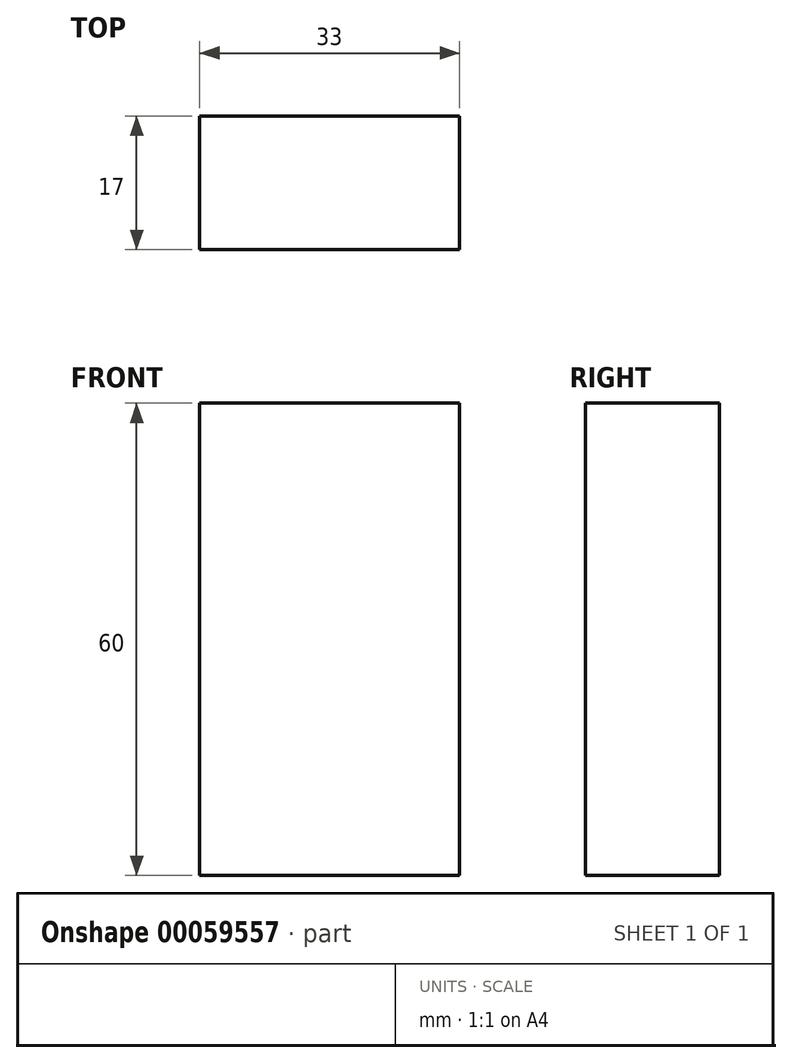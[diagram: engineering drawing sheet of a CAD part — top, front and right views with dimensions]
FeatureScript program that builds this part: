
annotation { "Feature Type Name" : "Feature", "Feature Type Description" : "" }
export const myFeature = defineFeature(function(context is Context, id is Id, definition is map)
    precondition{}
    {
        {
            var Q0;
            Q0=qCreatedBy(makeId("Front.planeOp"),FACE);
            var sketch = newSketch(context, id + "F0", { "sketchPlane" : qUnion([Q0])});
            skLineSegment(sketch, "E0.bottom", {"start": v(-16.5, 30) * mm, "end": v(16.5, 30) * mm});
            skLineSegment(sketch, "E0.top", {"start": v(-16.5, -30) * mm, "end": v(16.5, -30) * mm});
            skLineSegment(sketch, "E0.left", {"start": v(-16.5, 30) * mm, "end": v(-16.5, -30) * mm});
            skLineSegment(sketch, "E0.right", {"start": v(16.5, 30) * mm, "end": v(16.5, -30) * mm});
            skPoint(sketch, "E0.middle", {"position": v(0, 0) * mm});
            skSolve(sketch);
        }
        {
            var Q0;
            Q0 = qSketchRegion(id + "F0", true);
            extrude(context, id + "F1", {"entities" : qUnion([Q0]), "depth" : 17 * mm});
        }
    });
